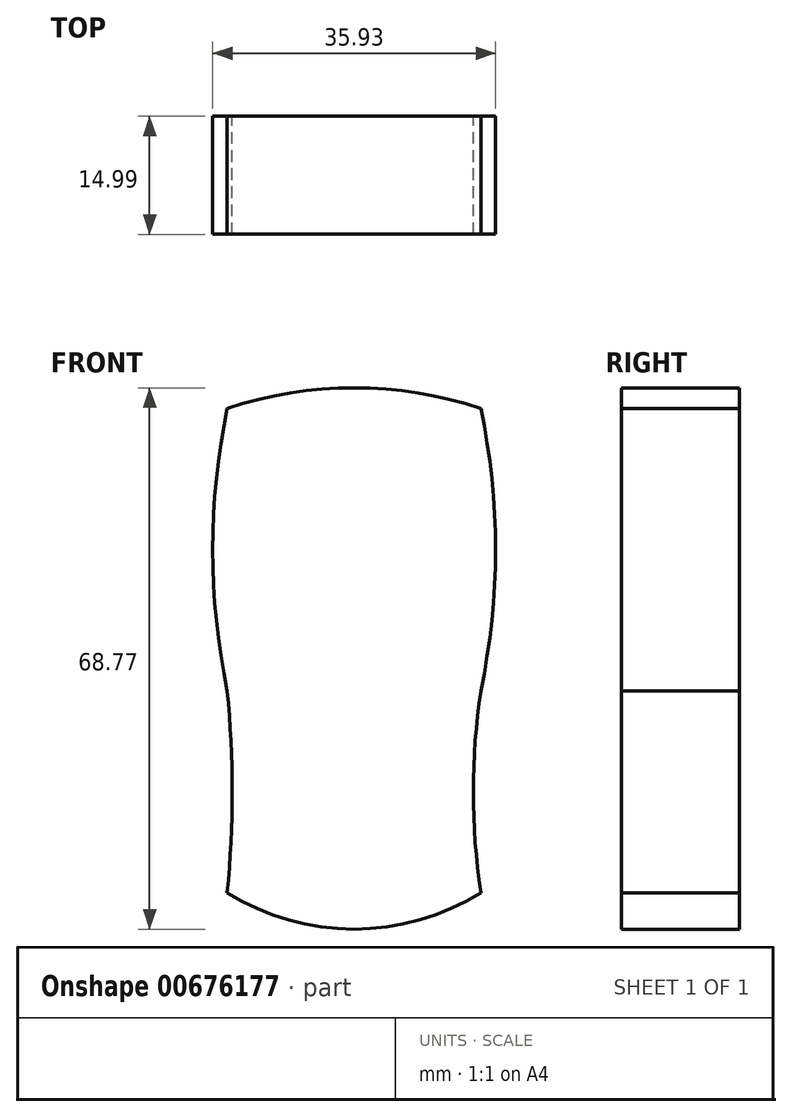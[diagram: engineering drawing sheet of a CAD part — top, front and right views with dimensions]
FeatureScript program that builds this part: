
annotation { "Feature Type Name" : "Feature", "Feature Type Description" : "" }
export const myFeature = defineFeature(function(context is Context, id is Id, definition is map)
    precondition{}
    {
        {
            var Q0;
            Q0=qCreatedBy(makeId("Front.planeOp"),FACE);
            var sketch = newSketch(context, id + "F0", { "sketchPlane" : qUnion([Q0])});
            skArc(sketch, "E0", {"start": v(-68.57, 0) * mm, "mid": v(-52.46, -4.64) * mm, "end": v(-36.35, 0) * mm});
            skArc(sketch, "E1", {"start": v(-36.35, 25.65) * mm, "mid": v(-37.3, 12.83) * mm, "end": v(-36.35, 0) * mm});
            skArc(sketch, "E2", {"start": v(-68.57, 0) * mm, "mid": v(-67.93, 12.83) * mm, "end": v(-68.57, 25.65) * mm});
            skArc(sketch, "E3", {"start": v(-68.57, 61.5) * mm, "mid": v(-70.4, 43.58) * mm, "end": v(-68.57, 25.65) * mm});
            skArc(sketch, "E4", {"start": v(-36.35, 25.65) * mm, "mid": v(-34.48, 43.58) * mm, "end": v(-36.35, 61.5) * mm});
            skArc(sketch, "E5", {"start": v(-36.35, 61.5) * mm, "mid": v(-52.46, 64.13) * mm, "end": v(-68.57, 61.5) * mm});
            skSolve(sketch);
        }
        {
            var Q0;
            Q0=makeQuery(id+"F0.imprint","IMPRINT",FACE,{"disambiguationData":[TD([[makeQuery(id+"F0.imprint","IMPRINT",EDGE,{"derivedFrom":sQuery(id+"F0.wireOp",EDGE,"E0")}),1.0]])]});
            extrude(context, id + "F1", {"entities" : qUnion([Q0]), "depth" : 15 * mm, "offsetDistance" : 25.4 * mm});
        }
    });
